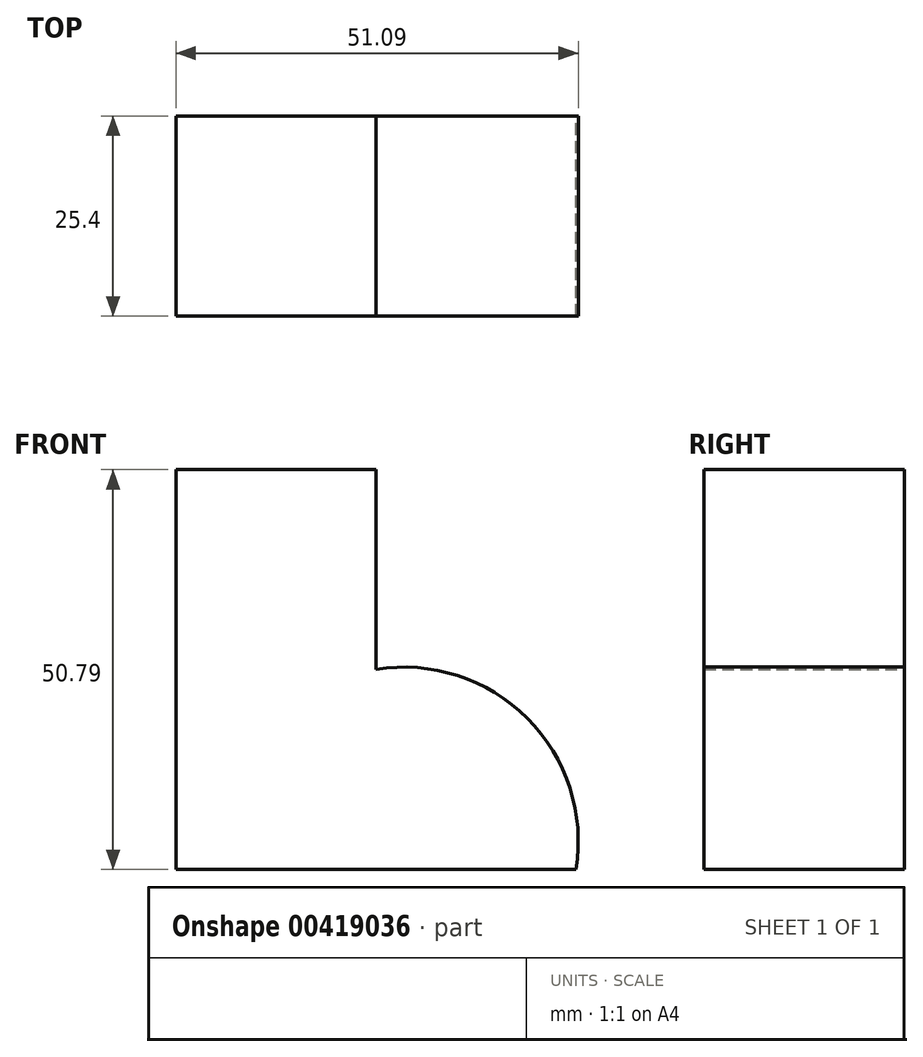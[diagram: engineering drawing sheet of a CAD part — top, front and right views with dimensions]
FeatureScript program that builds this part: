
annotation { "Feature Type Name" : "Feature", "Feature Type Description" : "" }
export const myFeature = defineFeature(function(context is Context, id is Id, definition is map)
    precondition{}
    {
        {
            var Q0;
            Q0=qCreatedBy(makeId("Front.planeOp"),FACE);
            var sketch = newSketch(context, id + "F0", { "sketchPlane" : qUnion([Q0])});
            skLineSegment(sketch, "E0", {"start": v(0, 0) * mm, "end": v(-50.8, 0) * mm});
            skLineSegment(sketch, "E1", {"start": v(-50.8, 0) * mm, "end": v(-50.8, 50.8) * mm});
            skLineSegment(sketch, "E2", {"start": v(-50.8, 50.8) * mm, "end": v(-25.4, 50.8) * mm});
            skLineSegment(sketch, "E3", {"start": v(-25.4, 50.8) * mm, "end": v(-25.4, 25.4) * mm});
            skArc(sketch, "E4", {"start": v(0, 0) * mm, "mid": v(-6.19, 19.2) * mm, "end": v(-25.4, 25.4) * mm});
            skSolve(sketch);
        }
        {
            var Q0;
            Q0=makeQuery(id+"F0.imprint","IMPRINT",FACE,{"disambiguationData":[TD([[makeQuery(id+"F0.imprint","IMPRINT",EDGE,{"derivedFrom":sQuery(id+"F0.wireOp",EDGE,"E0")}),-1.0]])]});
            extrude(context, id + "F1", {"entities" : qUnion([Q0]), "depth" : 25.4 * mm});
        }
    });
